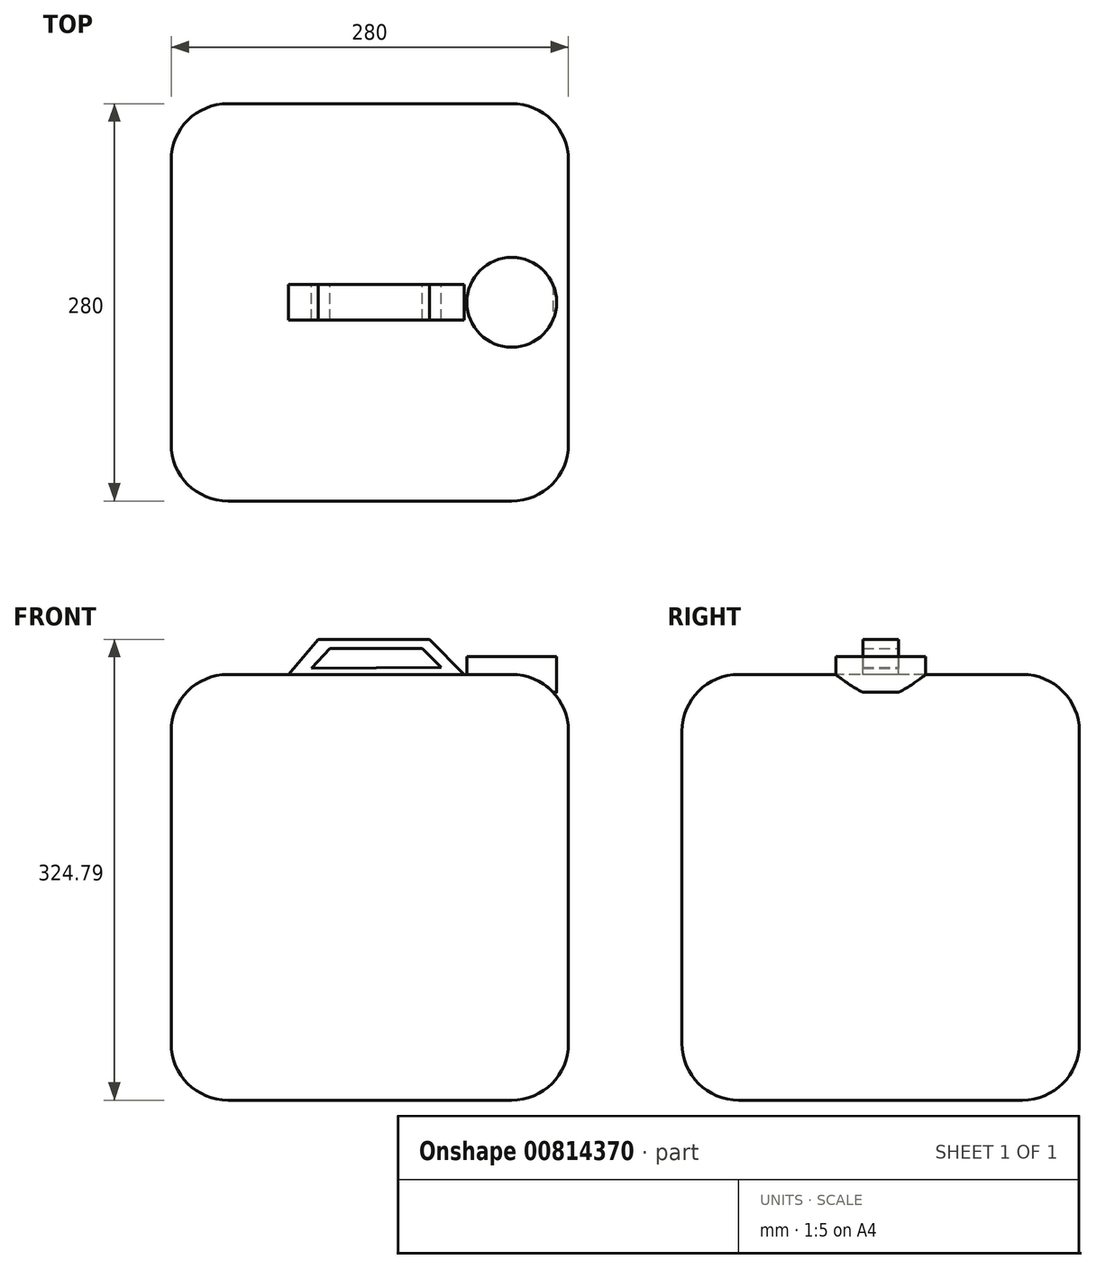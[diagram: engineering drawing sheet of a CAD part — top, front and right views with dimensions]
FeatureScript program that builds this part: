
annotation { "Feature Type Name" : "Feature", "Feature Type Description" : "" }
export const myFeature = defineFeature(function(context is Context, id is Id, definition is map)
    precondition{}
    {
        {
            var Q0;
            Q0=qCreatedBy(makeId("Top.planeOp"),FACE);
            var sketch = newSketch(context, id + "F0", { "sketchPlane" : qUnion([Q0])});
            skLineSegment(sketch, "E0.bottom", {"start": v(100, 140) * mm, "end": v(-100, 140) * mm});
            skLineSegment(sketch, "E0.top", {"start": v(100, -140) * mm, "end": v(-100, -140) * mm});
            skLineSegment(sketch, "E0.left", {"start": v(140, 100) * mm, "end": v(140, -100) * mm});
            skLineSegment(sketch, "E0.right", {"start": v(-140, 100) * mm, "end": v(-140, -100) * mm});
            skPoint(sketch, "E0.middle", {"position": v(0, 0) * mm});
            skPoint(sketch, "E1.visualSharp", {"position": v(-140, -140) * mm});
            skArc(sketch, "E1.filletArc", {"start": v(-140, -100) * mm, "mid": v(-128.28, -128.28) * mm, "end": v(-100, -140) * mm});
            skPoint(sketch, "E2.visualSharp", {"position": v(-140, 140) * mm});
            skArc(sketch, "E2.filletArc", {"start": v(-100, 140) * mm, "mid": v(-128.28, 128.28) * mm, "end": v(-140, 100) * mm});
            skPoint(sketch, "E3.visualSharp", {"position": v(140, -140) * mm});
            skArc(sketch, "E3.filletArc", {"start": v(100, -140) * mm, "mid": v(128.28, -128.28) * mm, "end": v(140, -100) * mm});
            skPoint(sketch, "E4.visualSharp", {"position": v(140, 140) * mm});
            skArc(sketch, "E4.filletArc", {"start": v(140, 100) * mm, "mid": v(128.28, 128.28) * mm, "end": v(100, 140) * mm});
            skLineSegment(sketch, "E5", {"start": v(140, 0) * mm, "end": v(75.65, 0) * mm, "construction": true});
            skCircle(sketch, "E6", {"center": v(75.65, 0) * mm, "radius": 35.1 * mm, "construction": true});
            skSolve(sketch);
        }
        {
            var Q0;
            Q0 = qSketchRegion(id + "F0", true);
            var Q1;
            Q1=makeQuery(id+"F0.imprint","IMPRINT",FACE,{"disambiguationData":[TD([[makeQuery(id+"F0.imprint","IMPRINT",EDGE,{"derivedFrom":sQuery(id+"F0.wireOp",EDGE,"E0.bottom")}),1.0]])]});
            extrude(context, id + "F1", {"entities" : qUnion([Q0, Q1]), "depth" : 300 * mm, "offsetDistance" : 25 * mm});
        }
        {
            var Q0;
            Q0=makeQuery(id+"F1.opExtrude","CAP_FACE",FACE,{"disambiguationData":[OSD([sQuery(id+"F0.wireOp",EDGE,"E0.bottom"),sQuery(id+"F0.wireOp",EDGE,"E0.top"),sQuery(id+"F0.wireOp",EDGE,"E0.left"),sQuery(id+"F0.wireOp",EDGE,"E0.right"),sQuery(id+"F0.wireOp",EDGE,"E1.filletArc"),sQuery(id+"F0.wireOp",EDGE,"E2.filletArc"),sQuery(id+"F0.wireOp",EDGE,"E3.filletArc"),sQuery(id+"F0.wireOp",EDGE,"E4.filletArc")])],"isStart":false});
            var Q1;
            Q1=makeQuery(id+"F1.opExtrude","CAP_EDGE",EDGE,{"disambiguationData":[OSD([sQuery(id+"F0.wireOp",EDGE,"E0.left")])],"isStart":true});
            fillet(context, id + "F2", {"entities" : qUnion([Q0, Q1]), "radius" : 40 * mm, "tangentPropagation" : true, "allowEdgeOverflow" : false});
        }
        {
            var Q0;
            Q0=makeQuery(id+"F1.opExtrude","CAP_FACE",FACE,{"disambiguationData":[OSD([sQuery(id+"F0.wireOp",EDGE,"E0.bottom"),sQuery(id+"F0.wireOp",EDGE,"E0.top"),sQuery(id+"F0.wireOp",EDGE,"E0.left"),sQuery(id+"F0.wireOp",EDGE,"E0.right"),sQuery(id+"F0.wireOp",EDGE,"E1.filletArc"),sQuery(id+"F0.wireOp",EDGE,"E2.filletArc"),sQuery(id+"F0.wireOp",EDGE,"E3.filletArc"),sQuery(id+"F0.wireOp",EDGE,"E4.filletArc")])],"isStart":false});
            var sketch = newSketch(context, id + "F3", { "sketchPlane" : qUnion([Q0])});
            skCircle(sketch, "E7", {"center": v(100, 0) * mm, "radius": 31.68 * mm});
            skSolve(sketch);
        }
        {
            var Q0;
            {var subQ0=sQuery(id+"F3.wireOp",EDGE,"E7");var subQ1=sQuery(id+"F0.wireOp",EDGE,"E0.left");var subQ2=makeQuery(id+"F2.opFillet","BLEND_EDGE",EDGE,{"blendedFrom":[makeQuery(id+"F1.opExtrude","CAP_EDGE",EDGE,{"disambiguationData":[OSD([subQ1])],"isStart":false}),makeQuery(id+"F1.opExtrude","CAP_FACE",FACE,{"disambiguationData":[OSD([sQuery(id+"F0.wireOp",EDGE,"E0.bottom"),sQuery(id+"F0.wireOp",EDGE,"E0.top"),subQ1,sQuery(id+"F0.wireOp",EDGE,"E0.right"),sQuery(id+"F0.wireOp",EDGE,"E1.filletArc"),sQuery(id+"F0.wireOp",EDGE,"E2.filletArc"),sQuery(id+"F0.wireOp",EDGE,"E3.filletArc"),sQuery(id+"F0.wireOp",EDGE,"E4.filletArc")])],"isStart":false})],"blendedInto":[makeQuery(id+"F1.opExtrude","CAP_FACE",FACE,{"disambiguationData":[OSD([sQuery(id+"F0.wireOp",EDGE,"E0.bottom"),sQuery(id+"F0.wireOp",EDGE,"E0.top"),subQ1,sQuery(id+"F0.wireOp",EDGE,"E0.right"),sQuery(id+"F0.wireOp",EDGE,"E1.filletArc"),sQuery(id+"F0.wireOp",EDGE,"E2.filletArc"),sQuery(id+"F0.wireOp",EDGE,"E3.filletArc"),sQuery(id+"F0.wireOp",EDGE,"E4.filletArc")])],"isStart":false})]});var subQ3=makeQuery(id+"F3.imprint","INTERSECT",VERTEX,{"disambiguationData":[OD(0.0)],"derivedFrom":[subQ2,subQ0]});Q0=makeQuery(id+"F3.imprint","IMPRINT",FACE,{"disambiguationData":[TD([[makeQuery(id+"F3.imprint","IMPRINT",EDGE,{"disambiguationData":[TD([[subQ3,-1.0]])],"derivedFrom":subQ0}),1.0]])]});}
            var Q1;
            {var subQ0=sQuery(id+"F3.wireOp",EDGE,"E7");var subQ1=sQuery(id+"F0.wireOp",EDGE,"E0.left");var subQ2=makeQuery(id+"F2.opFillet","BLEND_EDGE",EDGE,{"blendedFrom":[makeQuery(id+"F1.opExtrude","CAP_EDGE",EDGE,{"disambiguationData":[OSD([subQ1])],"isStart":false}),makeQuery(id+"F1.opExtrude","CAP_FACE",FACE,{"disambiguationData":[OSD([sQuery(id+"F0.wireOp",EDGE,"E0.bottom"),sQuery(id+"F0.wireOp",EDGE,"E0.top"),subQ1,sQuery(id+"F0.wireOp",EDGE,"E0.right"),sQuery(id+"F0.wireOp",EDGE,"E1.filletArc"),sQuery(id+"F0.wireOp",EDGE,"E2.filletArc"),sQuery(id+"F0.wireOp",EDGE,"E3.filletArc"),sQuery(id+"F0.wireOp",EDGE,"E4.filletArc")])],"isStart":false})],"blendedInto":[makeQuery(id+"F1.opExtrude","CAP_FACE",FACE,{"disambiguationData":[OSD([sQuery(id+"F0.wireOp",EDGE,"E0.bottom"),sQuery(id+"F0.wireOp",EDGE,"E0.top"),subQ1,sQuery(id+"F0.wireOp",EDGE,"E0.right"),sQuery(id+"F0.wireOp",EDGE,"E1.filletArc"),sQuery(id+"F0.wireOp",EDGE,"E2.filletArc"),sQuery(id+"F0.wireOp",EDGE,"E3.filletArc"),sQuery(id+"F0.wireOp",EDGE,"E4.filletArc")])],"isStart":false})]});var subQ3=makeQuery(id+"F3.imprint","INTERSECT",VERTEX,{"disambiguationData":[OD(0.0)],"derivedFrom":[subQ2,subQ0]});Q1=makeQuery(id+"F3.imprint","IMPRINT",FACE,{"disambiguationData":[TD([[makeQuery(id+"F3.imprint","IMPRINT",EDGE,{"disambiguationData":[TD([[subQ3,1.0]])],"derivedFrom":subQ0}),1.0]])]});}
            extrude(context, id + "F4", {"entities" : qUnion([Q0, Q1]), "operationType" : NewBodyOperationType.ADD, "depth" : 25 * mm, "offsetDistance" : 25 * mm, "symmetric" : true});
        }
        {
            var Q0;
            Q0=qCreatedBy(makeId("Front.planeOp"),FACE);
            var sketch = newSketch(context, id + "F5", { "sketchPlane" : qUnion([Q0])});
            skLineSegment(sketch, "E8", {"start": v(-57.62, 299.74) * mm, "end": v(-36.39, 324.79) * mm});
            skLineSegment(sketch, "E9", {"start": v(-36.39, 324.79) * mm, "end": v(42.06, 324.79) * mm});
            skLineSegment(sketch, "E10", {"start": v(42.06, 324.79) * mm, "end": v(66.63, 299.74) * mm});
            skLineSegment(sketch, "E11", {"start": v(66.63, 299.74) * mm, "end": v(-61.9, 299.74) * mm});
            skLineSegment(sketch, "E12", {"start": v(-40.98, 304.27) * mm, "end": v(-28.13, 318.38) * mm});
            skLineSegment(sketch, "E13", {"start": v(-28.13, 318.38) * mm, "end": v(37.1, 318.38) * mm});
            skLineSegment(sketch, "E14", {"start": v(37.1, 318.38) * mm, "end": v(50.28, 304.94) * mm});
            skLineSegment(sketch, "E15", {"start": v(50.28, 304.94) * mm, "end": v(-40.98, 304.27) * mm});
            skSolve(sketch);
        }
        {
            var Q0;
            {var subQ1=sQuery(id+"F5.wireOp",EDGE,"E8");Q0=makeQuery(id+"F5.imprint","IMPRINT",FACE,{"disambiguationData":[TD([[makeQuery(id+"F5.imprint","IMPRINT",EDGE,{"derivedFrom":subQ1}),-1.0]])]});}
            extrude(context, id + "F6", {"entities" : qUnion([Q0]), "operationType" : NewBodyOperationType.ADD, "depth" : 25 * mm, "offsetDistance" : 25 * mm, "symmetric" : true});
        }
    });
